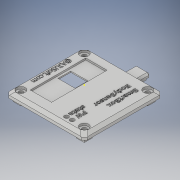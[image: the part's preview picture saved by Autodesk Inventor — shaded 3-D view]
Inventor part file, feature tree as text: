
AUTODESK INVENTOR PART (.ipt)
format: ipt  version: 2019 (Build 230136000, 136)  size: 1,418,752 bytes
history: native  units: mm
features: move_body x16, sketch x13, extrude x12, direct_edit x10, chamfer x3
ambient origin geometry x8: Origin, YZ Plane, XZ Plane, XY Plane, X Axis, Y Axis, Z Axis, Center Point
bodies: Solid1 (feature_tree)
feature tree (54):
  extrude  "Extrusion1"  Depth=55.0mm
  extrude  "Extrusion2"  Depth=50.0mm
  extrude  "Extrusion3"  Depth=2.0mm TaperAngle=0.0deg
  sketch  "Sketch4"  dims[d8=5.5mm d9=5.5mm]
  extrude  "Extrusion4"  Depth=5.5mm
  extrude  "Extrusion5"  Depth=5.5mm
  direct_edit  "Direct Edit1"
  direct_edit  "Direct Edit2"
  extrude  "Extrusion6"  Depth=5.5mm
  extrude  "Extrusion7"  Depth=5.5mm
  extrude  "Extrusion8"  Depth=1.2mm TaperAngle=0.0deg
  extrude  "Extrusion9"  TaperAngle=0.0deg  [1 undecoded]
  direct_edit  "Direct Edit3"
  extrude  "Extrusion10"  TaperAngle=0.0deg  [1 undecoded]
  direct_edit  "Direct Edit4"
  direct_edit  "Direct Edit5"
  direct_edit  "Direct Edit6"
  direct_edit  "Direct Edit7"
  direct_edit  "Direct Edit8"
  direct_edit  "Direct Edit9"
  extrude  "Extrusion11"  Depth=3.0mm
  extrude  "Extrusion12"  Depth=4.0mm TaperAngle=0.0deg
  chamfer  "Chamfer1"  Distance=8.0mm
  chamfer  "Chamfer2"  Distance=5.3mm
  chamfer  "Chamfer3"  Distance=0.7mm
  direct_edit  "Direct Edit10"
  sketch  "Sketch1"  dims[d0=55.0mm d1=55.0mm]
  sketch  "Sketch2"  dims[d2=7.0mm d3=0.0mm d4=50.0mm]
  sketch  "Sketch3"  dims[d5=50.0mm d6=2.0mm d7=0.0mm]
  sketch  "Sketch5"  dims[d10=5.5mm d11=5.5mm]
  sketch  "Sketch6"  dims[d12=5.5mm d13=5.5mm]
  sketch  "Sketch7"  dims[d14=5.5mm d15=5.5mm]
  sketch  "Sketch8"  dims[d16=5.0mm d17=0.0mm d18=1.2mm d19=0.0mm]
  sketch  "Sketch9"  dims[d20=3.0mm d21=0.0mm d22=0.0mm d23=0.0mm d24=-4.75mm]
  sketch  "Sketch10"  dims[d25=0.0mm d26=0.0mm d27=-3.0mm d28=0.0mm d29=0.0mm d30=-3.0mm]
  sketch  "Sketch11"  dims[d31=3.0mm d32=3.0mm]
  sketch  "Sketch12"  dims[d33=3.0mm d34=0.0mm d35=4.0mm d36=0.0mm]
  sketch  "Sketch13"  dims[d37=2.0mm d38=8.0mm d39=0.0mm d40=5.3mm d41=0.7mm d42=0.0mm d43=0.0mm d44=0.0mm d45=-0.5mm d46=0.0mm d47=0.0mm d48=0.5mm d49=0.6mm d50=0.0mm d51=0.0mm d52=0.0mm d53=-2.5mm d54=0.0mm d55=0.0mm d56=2.5mm d57=-1.0mm d58=0.0mm d59=0.0mm d60=0.0mm d61=0.0mm d62=-1.75mm d63=0.0mm d64=0.0mm d65=-0.75mm d66=0.0mm d67=0.0mm d68=0.75mm d69=0.0mm d70=0.0mm d71=0.75mm d72=0.0mm d73=0.0mm d74=-1.0mm d75=0.0mm d76=0.0mm d77=-1.0mm d78=3.889mm d79=3.889mm d80=3.889mm d81=45.0deg d82=3.8885mm d83=3.0mm d84=3.0mm d85=3.0mm d86=3.0mm d87=10.0mm d88=0.0mm d89=6.0mm d90=6.0mm d91=6.0mm d92=6.0mm d93=1.5mm d94=0.0mm d95=2.0mm d96=2.0mm d97=45.0deg d98=2.0mm d99=2.0mm d100=45.0deg d101=1.2mm d102=2.0mm d103=45.0deg d104=0.0mm d105=0.0mm d106=-0.25mm d107=0.0mm d108=0.0mm d109=-0.25mm]
  move_body  "Move1"
  move_body  "Move2"
  move_body  "Move3"
  move_body  "Move4"
  move_body  "Move5"
  move_body  "Move6"
  move_body  "Move7"
  move_body  "Move8"
  move_body  "Move9"
  move_body  "Move10"
  move_body  "Move11"
  move_body  "Move12"
  move_body  "Move13"
  move_body  "Move14"
  move_body  "Move15"
  move_body  "Move16"
note: 2 required parameter values undecoded (feature->parameter linkage not recoverable at this tier; creation-order binding heuristic only, values carry confidence <= 0.55)
